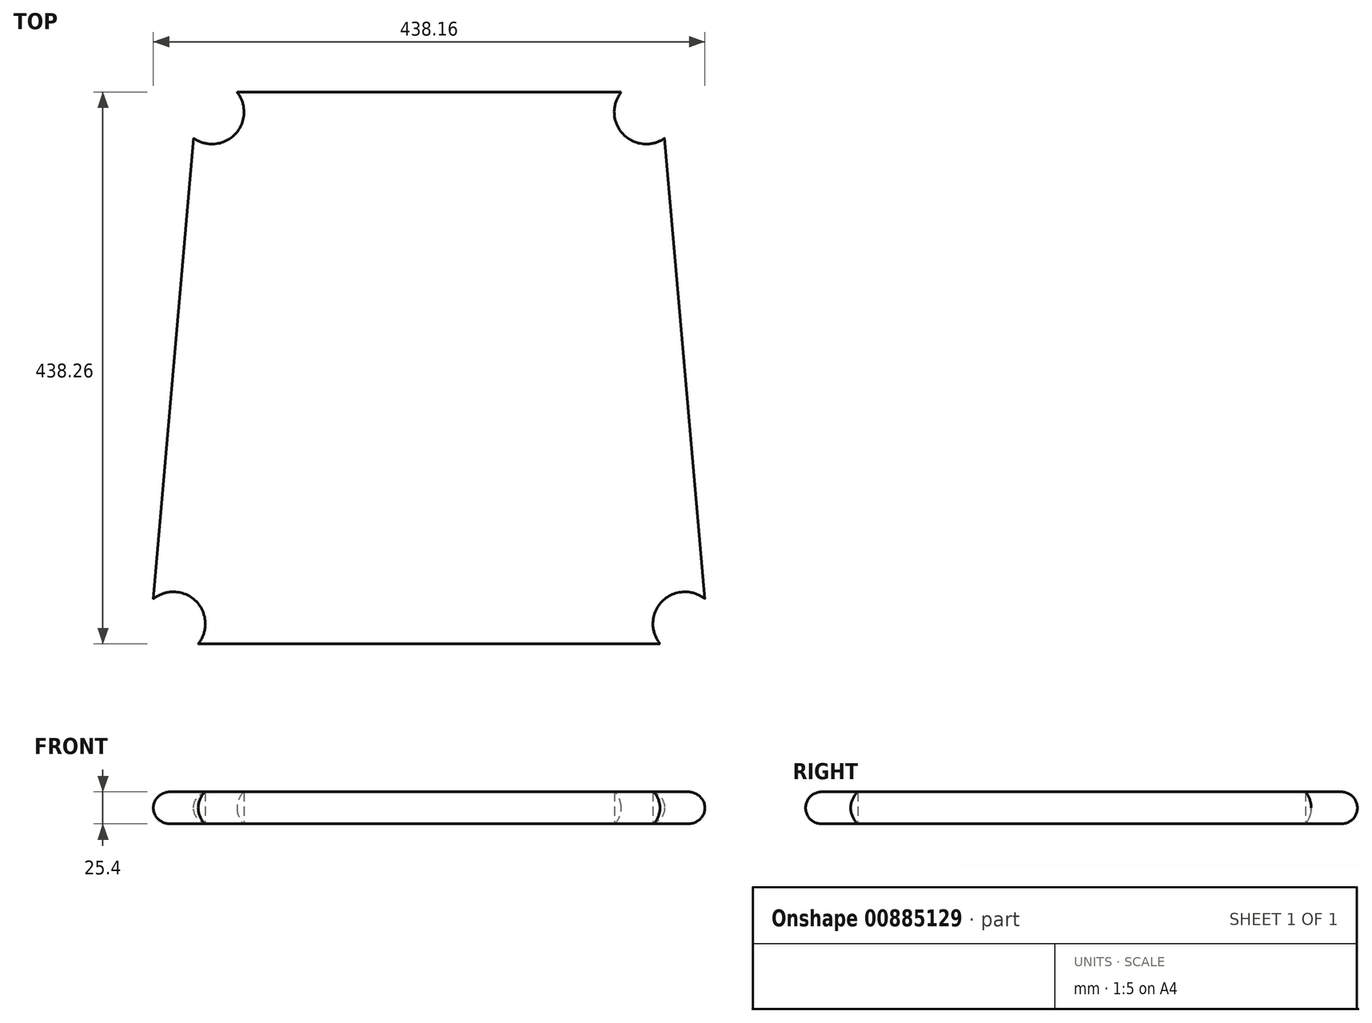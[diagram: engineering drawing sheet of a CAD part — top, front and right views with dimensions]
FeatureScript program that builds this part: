
annotation { "Feature Type Name" : "Feature", "Feature Type Description" : "" }
export const myFeature = defineFeature(function(context is Context, id is Id, definition is map)
    precondition{}
    {
        {
            var Q0;
            Q0=qCreatedBy(makeId("Top.planeOp"),FACE);
            var sketch = newSketch(context, id + "F0", { "sketchPlane" : qUnion([Q0])});
            skArc(sketch, "E0", {"start": v(-183.46, -219.18) * mm, "mid": v(-185.2, -185.29) * mm, "end": v(-219.07, -183.37) * mm});
            skArc(sketch, "E1", {"start": v(219.08, -183.37) * mm, "mid": v(185.2, -185.29) * mm, "end": v(183.46, -219.18) * mm});
            skArc(sketch, "E2", {"start": v(152.64, 219.08) * mm, "mid": v(153.95, 185.8) * mm, "end": v(187.07, 182.42) * mm});
            skArc(sketch, "E3", {"start": v(-187.07, 182.42) * mm, "mid": v(-153.95, 185.8) * mm, "end": v(-152.64, 219.08) * mm});
            skLineSegment(sketch, "E4", {"start": v(-203.2, -203.2) * mm, "end": v(-203.2, -203.2) * mm});
            skLineSegment(sketch, "E5", {"start": v(219.08, -183.37) * mm, "end": v(187.07, 182.42) * mm});
            skLineSegment(sketch, "E6", {"start": v(152.64, 219.08) * mm, "end": v(-152.64, 219.07) * mm});
            skLineSegment(sketch, "E7", {"start": v(-183.46, -219.18) * mm, "end": v(183.46, -219.18) * mm});
            skLineSegment(sketch, "E8", {"start": v(-187.07, 182.42) * mm, "end": v(-219.08, -183.37) * mm});
            skSolve(sketch);
        }
        {
            var Q0;
            Q0 = qSketchRegion(id + "F0", true);
            extrude(context, id + "F1", {"entities" : qUnion([Q0]), "depth" : 25.4 * mm, "offsetDistance" : 25.4 * mm});
        }
        {
            var Q0;
            Q0=makeQuery(id+"F1.opExtrude","CAP_EDGE",EDGE,{"disambiguationData":[OSD([sQuery(id+"F0.wireOp",EDGE,"E8")])],"isStart":false});
            var Q1;
            Q1=makeQuery(id+"F1.opExtrude","CAP_EDGE",EDGE,{"disambiguationData":[OSD([sQuery(id+"F0.wireOp",EDGE,"E6")])],"isStart":false});
            var Q2;
            Q2=makeQuery(id+"F1.opExtrude","CAP_EDGE",EDGE,{"disambiguationData":[OSD([sQuery(id+"F0.wireOp",EDGE,"E7")])],"isStart":false});
            var Q3;
            Q3=makeQuery(id+"F1.opExtrude","CAP_EDGE",EDGE,{"disambiguationData":[OSD([sQuery(id+"F0.wireOp",EDGE,"E5")])],"isStart":false});
            var Q4;
            Q4=makeQuery(id+"F1.opExtrude","CAP_EDGE",EDGE,{"disambiguationData":[OSD([sQuery(id+"F0.wireOp",EDGE,"E8")])],"isStart":true});
            var Q5;
            Q5=makeQuery(id+"F1.opExtrude","CAP_EDGE",EDGE,{"disambiguationData":[OSD([sQuery(id+"F0.wireOp",EDGE,"E7")])],"isStart":true});
            var Q6;
            Q6=makeQuery(id+"F1.opExtrude","CAP_EDGE",EDGE,{"disambiguationData":[OSD([sQuery(id+"F0.wireOp",EDGE,"E6")])],"isStart":true});
            var Q7;
            Q7=makeQuery(id+"F1.opExtrude","CAP_EDGE",EDGE,{"disambiguationData":[OSD([sQuery(id+"F0.wireOp",EDGE,"E5")])],"isStart":true});
            fillet(context, id + "F2", {"entities" : qUnion([Q0, Q1, Q2, Q3, Q4, Q5, Q6, Q7]), "radius" : 12.7 * mm, "tangentPropagation" : true, "allowEdgeOverflow" : false});
        }
    });
